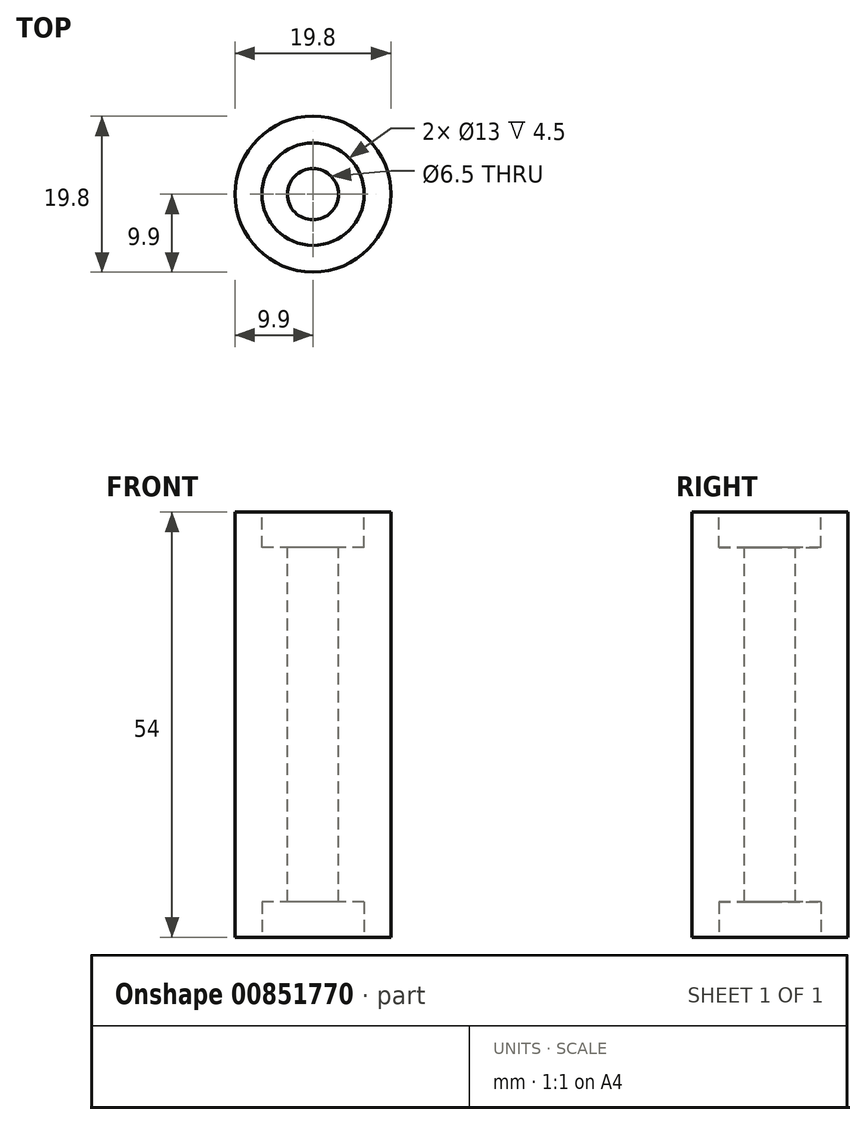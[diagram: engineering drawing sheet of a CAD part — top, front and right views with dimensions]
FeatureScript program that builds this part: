
annotation { "Feature Type Name" : "Feature", "Feature Type Description" : "" }
export const myFeature = defineFeature(function(context is Context, id is Id, definition is map)
    precondition{}
    {
        {
            assignVariable(context, id + "F0", {"name" : "RollerWidth", "anyValue" : 54 * mm});
        }
        {
            assignVariable(context, id + "F1", {"name" : "BearingWidth", "anyValue" : 4.5 * mm});
        }
        {
            var Q0;
            Q0=qCreatedBy(makeId("Top.planeOp"),FACE);
            var sketch = newSketch(context, id + "F2", { "sketchPlane" : qUnion([Q0])});
            skCircle(sketch, "E0", {"center": v(0, 0) * mm, "radius": 9.9 * mm});
            skSolve(sketch);
        }
        {
            var Q0;
            Q0 = qSketchRegion(id + "F2", true);
            extrude(context, id + "F3", {"entities" : qUnion([Q0]), "depth" : getVariable(context, 'RollerWidth') / 2, "offsetDistance" : 25 * mm});
        }
        {
            var Q0;
            Q0=makeQuery(id+"F3.opExtrude","CAP_FACE",FACE,{"disambiguationData":[OSD([sQuery(id+"F2.wireOp",EDGE,"E0")])],"isStart":false});
            var sketch = newSketch(context, id + "F4", { "sketchPlane" : qUnion([Q0])});
            skCircle(sketch, "E1", {"center": v(0, 0) * mm, "radius": 6.5 * mm});
            skSolve(sketch);
        }
        {
            var Q0;
            Q0=makeQuery(id+"F4.imprint","IMPRINT",FACE,{"disambiguationData":[TD([[makeQuery(id+"F4.imprint","IMPRINT",EDGE,{"derivedFrom":sQuery(id+"F4.wireOp",EDGE,"E1")}),1.0]])]});
            extrude(context, id + "F5", {"entities" : qUnion([Q0]), "operationType" : NewBodyOperationType.REMOVE, "oppositeDirection" : true, "depth" : getVariable(context, 'BearingWidth'), "offsetDistance" : 25 * mm});
        }
        {
            var Q0;
            Q0=makeQuery(id+"F5.boolean.opBoolean","COPY",FACE,{"derivedFrom":makeQuery(id+"F5.opExtrude","CAP_FACE",FACE,{"disambiguationData":[OSD([sQuery(id+"F4.wireOp",EDGE,"E1")])],"isStart":false})});
            var sketch = newSketch(context, id + "F6", { "sketchPlane" : qUnion([Q0])});
            skCircle(sketch, "E2", {"center": v(0, 0) * mm, "radius": 3.25 * mm});
            skSolve(sketch);
        }
        {
            var Q0;
            Q0=makeQuery(id+"F6.imprint","IMPRINT",FACE,{"disambiguationData":[TD([[makeQuery(id+"F6.imprint","IMPRINT",EDGE,{"derivedFrom":sQuery(id+"F6.wireOp",EDGE,"E2")}),1.0]])]});
            extrude(context, id + "F7", {"entities" : qUnion([Q0]), "operationType" : NewBodyOperationType.REMOVE, "endBound" : BoundingType.THROUGH_ALL, "oppositeDirection" : true, "depth" : 25 * mm, "offsetDistance" : 25 * mm});
        }
        {
            var Q0;
            Q0=makeQuery(id+"F3.opExtrude","SWEPT_BODY",BODY,{"disambiguationData":[OSD([sQuery(id+"F2.wireOp",EDGE,"E0")])]});
            var Q1;
            Q1=qCreatedBy(makeId("Top.planeOp"),FACE);
            mirror(context, id + "F8", {"operationType" : NewBodyOperationType.ADD, "entities" : qUnion([Q0]), "mirrorPlane" : qUnion([Q1])});
        }
    });
